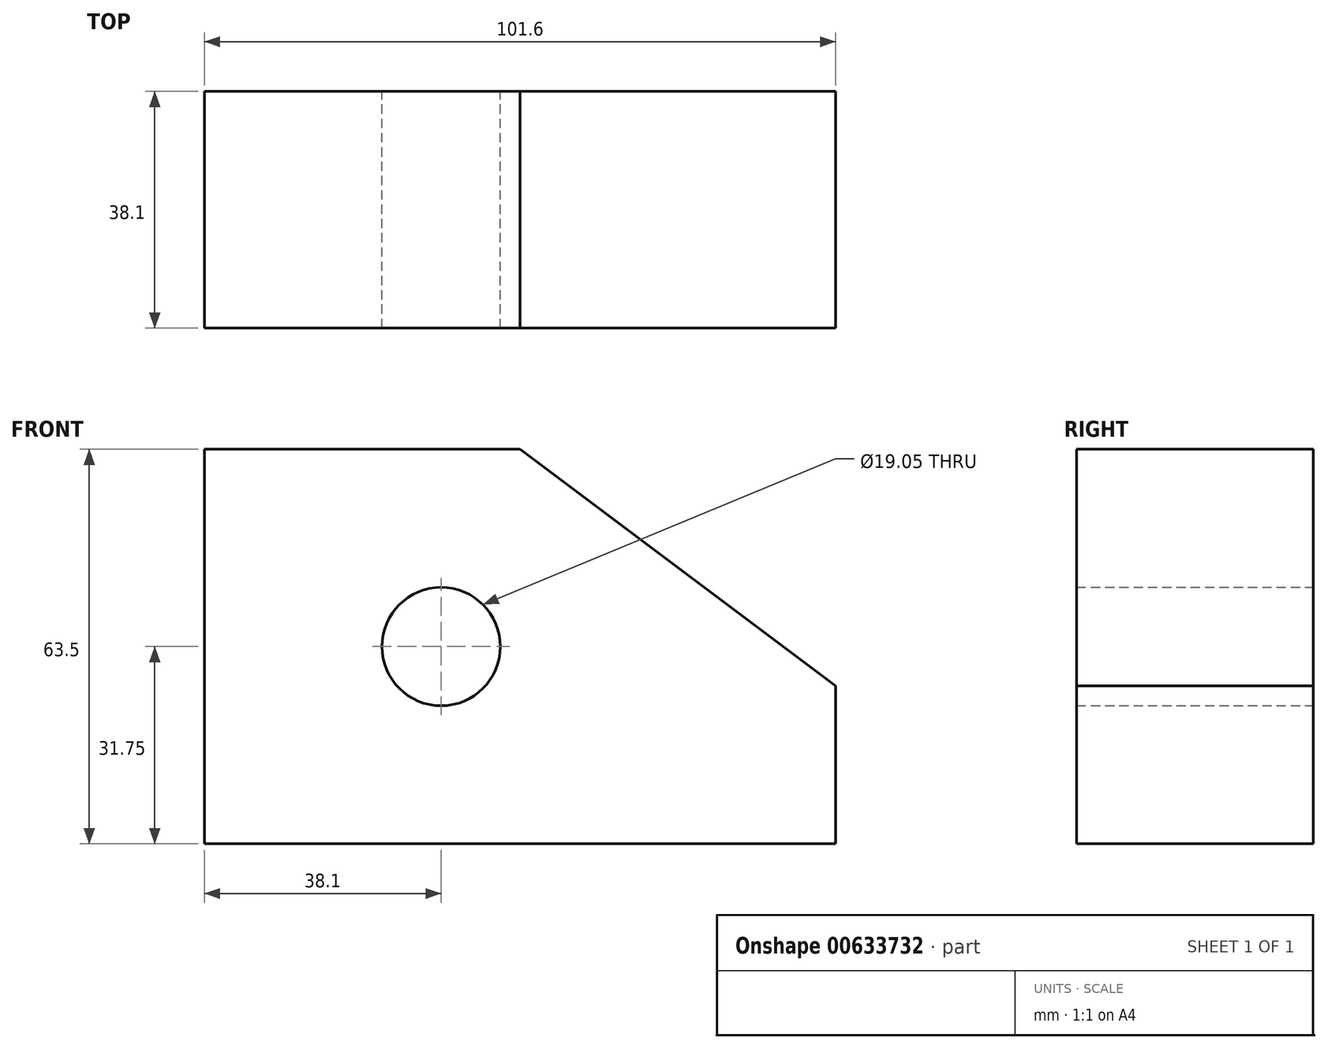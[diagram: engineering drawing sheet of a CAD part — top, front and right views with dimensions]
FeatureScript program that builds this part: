
annotation { "Feature Type Name" : "Feature", "Feature Type Description" : "" }
export const myFeature = defineFeature(function(context is Context, id is Id, definition is map)
    precondition{}
    {
        {
            var Q0;
            Q0=qCreatedBy(makeId("Front.planeOp"),FACE);
            var sketch = newSketch(context, id + "F0", { "sketchPlane" : qUnion([Q0])});
            skLineSegment(sketch, "E0", {"start": v(0, 0) * mm, "end": v(101.6, 0) * mm});
            skLineSegment(sketch, "E1", {"start": v(101.6, 0) * mm, "end": v(101.6, 25.4) * mm});
            skLineSegment(sketch, "E2", {"start": v(0, 0) * mm, "end": v(0, 63.5) * mm});
            skLineSegment(sketch, "E3", {"start": v(0, 63.5) * mm, "end": v(50.8, 63.5) * mm});
            skLineSegment(sketch, "E4", {"start": v(50.8, 63.5) * mm, "end": v(101.6, 25.4) * mm});
            skCircle(sketch, "E5", {"center": v(38.1, 31.75) * mm, "radius": 9.53 * mm});
            skSolve(sketch);
        }
        {
            var Q0;
            Q0 = qSketchRegion(id + "F0", true);
            extrude(context, id + "F1", {"entities" : qUnion([Q0]), "depth" : 38.1 * mm, "offsetDistance" : 25.4 * mm});
        }
    });
